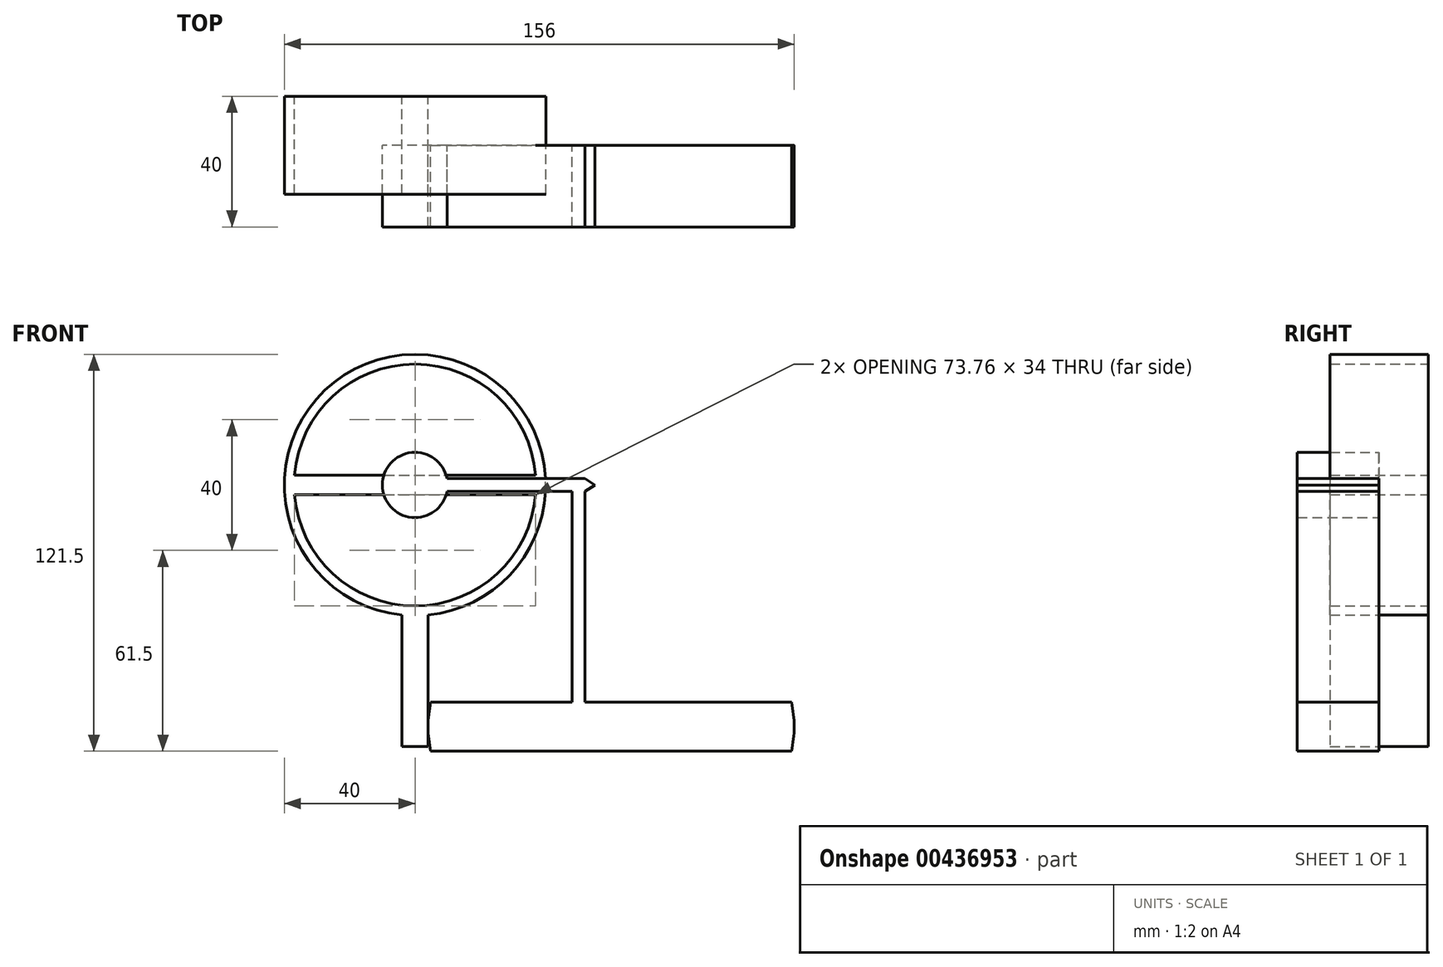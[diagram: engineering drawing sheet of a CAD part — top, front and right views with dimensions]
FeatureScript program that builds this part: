
annotation { "Feature Type Name" : "Feature", "Feature Type Description" : "" }
export const myFeature = defineFeature(function(context is Context, id is Id, definition is map)
    precondition{}
    {
        {
            var Q0;
            Q0=qCreatedBy(makeId("Front.planeOp"),FACE);
            var sketch = newSketch(context, id + "F0", { "sketchPlane" : qUnion([Q0])});
            skCircle(sketch, "E0", {"center": v(0, 0) * mm, "radius": 40 * mm});
            skLineSegment(sketch, "E1", {"start": v(-4, -39.8) * mm, "end": v(-4, -80) * mm});
            skLineSegment(sketch, "E2", {"start": v(-4, -80) * mm, "end": v(4, -80) * mm});
            skLineSegment(sketch, "E3", {"start": v(4, -80) * mm, "end": v(4, -39.8) * mm});
            skLineSegment(sketch, "E4", {"start": v(0, -40) * mm, "end": v(0, -94.92) * mm, "construction": true});
            skLineSegment(sketch, "E5", {"start": v(0, 71.87) * mm, "end": v(0, -94.92) * mm, "construction": true});
            skArc(sketch, "E6", {"start": v(-36.88, -3) * mm, "mid": v(0, -37) * mm, "end": v(36.88, -3) * mm});
            skLineSegment(sketch, "E7.bottom", {"start": v(-36.88, 3) * mm, "end": v(36.88, 3) * mm});
            skLineSegment(sketch, "E7.top", {"start": v(-36.88, -3) * mm, "end": v(36.88, -3) * mm});
            skArc(sketch, "E8.trimOffspring", {"start": v(36.88, 3) * mm, "mid": v(0, 37) * mm, "end": v(-36.88, 3) * mm});
            skLineSegment(sketch, "E9", {"start": v(-44.01, 0) * mm, "end": v(48.74, 0) * mm, "construction": true});
            skLineSegment(sketch, "E10", {"start": v(0, 0) * mm, "end": v(0, -40) * mm, "construction": true});
            skSolve(sketch);
        }
        {
            var Q0;
            Q0=makeQuery(id+"F0.imprint","IMPRINT",FACE,{"disambiguationData":[TD([[makeQuery(id+"F0.imprint","IMPRINT",EDGE,{"derivedFrom":sQuery(id+"F0.wireOp",EDGE,"E6")}),-1.0]])]});
            var Q1;
            {var subQ0=sQuery(id+"F0.wireOp",EDGE,"E1");Q1=makeQuery(id+"F0.imprint","IMPRINT",FACE,{"disambiguationData":[TD([[makeQuery(id+"F0.imprint","IMPRINT",EDGE,{"derivedFrom":subQ0}),1.0]])]});}
            extrude(context, id + "F1", {"entities" : qUnion([Q0, Q1]), "depth" : 30 * mm, "symmetric" : true});
        }
        {
            var Q0;
            Q0=qCreatedBy(makeId("Front.planeOp"),FACE);
            var sketch = newSketch(context, id + "F2", { "sketchPlane" : qUnion([Q0])});
            skArc(sketch, "E11", {"start": v(4.81, -66.5) * mm, "mid": v(4, -74) * mm, "end": v(4.81, -81.5) * mm});
            skCircle(sketch, "E12", {"center": v(0, 0) * mm, "radius": 10 * mm});
            skLineSegment(sketch, "E13", {"start": v(9.8, 2) * mm, "end": v(52, 2) * mm});
            skLineSegment(sketch, "E14", {"start": v(52, -2) * mm, "end": v(52, -66.5) * mm});
            skLineSegment(sketch, "E15", {"start": v(48, -2) * mm, "end": v(48, -66.5) * mm});
            skLineSegment(sketch, "E16", {"start": v(4, -48.62) * mm, "end": v(4, -148.23) * mm, "construction": true});
            skLineSegment(sketch, "E17", {"start": v(4.81, -81.5) * mm, "end": v(115.19, -81.5) * mm});
            skArc(sketch, "E18.trimOffspring", {"start": v(115.19, -81.5) * mm, "mid": v(116, -74) * mm, "end": v(115.19, -66.5) * mm});
            skLineSegment(sketch, "E19", {"start": v(39, -74) * mm, "end": v(14.11, -74) * mm, "construction": true});
            skLineSegment(sketch, "E20", {"start": v(4.81, -66.5) * mm, "end": v(115.19, -66.5) * mm});
            skLineSegment(sketch, "E21", {"start": v(52, 2) * mm, "end": v(55, 0) * mm});
            skLineSegment(sketch, "E22", {"start": v(55, 0) * mm, "end": v(52, -2) * mm});
            skLineSegment(sketch, "E23", {"start": v(55, 0) * mm, "end": v(45.5, 0) * mm, "construction": true});
            skLineSegment(sketch, "E24", {"start": v(48, -2) * mm, "end": v(9.8, -2) * mm});
            skSolve(sketch);
        }
        {
            var Q0;
            {var subQ4=sQuery(id+"F2.wireOp",EDGE,"E11");Q0=makeQuery(id+"F2.imprint","IMPRINT",FACE,{"disambiguationData":[TD([[makeQuery(id+"F2.imprint","IMPRINT",EDGE,{"derivedFrom":subQ4}),1.0]])]});}
            var Q1;
            {var subQ2=sQuery(id+"F2.wireOp",EDGE,"E13");Q1=makeQuery(id+"F2.imprint","IMPRINT",FACE,{"disambiguationData":[TD([[makeQuery(id+"F2.imprint","IMPRINT",EDGE,{"derivedFrom":subQ2}),-1.0]])]});}
            var Q2;
            {var subQ0=sQuery(id+"F2.wireOp",EDGE,"E12");var subQ1=makeQuery(id+"F2.imprint","INTERSECT",VERTEX,{"derivedFrom":[subQ0,sQuery(id+"F2.wireOp",EDGE,"E13")]});Q2=makeQuery(id+"F2.imprint","IMPRINT",FACE,{"disambiguationData":[TD([[makeQuery(id+"F2.imprint","IMPRINT",EDGE,{"disambiguationData":[TD([[subQ1,1.0]])],"derivedFrom":subQ0}),1.0]])]});}
            extrude(context, id + "F3", {"entities" : qUnion([Q0, Q1, Q2]), "depth" : 25 * mm});
        }
    });
